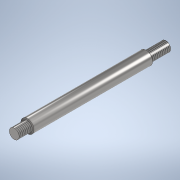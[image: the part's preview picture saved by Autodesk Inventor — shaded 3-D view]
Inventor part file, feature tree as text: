
AUTODESK INVENTOR PART (.ipt)
format: ipt  version: 2020 (Build 240168000, 168)  size: 111,104 bytes
history: native  units: mm
features: extrude x3, sketch x3, thread x1
ambient origin geometry x8: Origin, YZ Plane, XZ Plane, XY Plane, X Axis, Y Axis, Z Axis, Center Point
bodies: Solid1 (feature_tree)
feature tree (7):
  extrude  "Extrusion1"  Depth=6.0mm TaperAngle=0.0deg
  extrude  "Extrusion2"  Depth=36.0mm TaperAngle=0.0deg
  extrude  "Extrusion3"  Depth=4.0mm TaperAngle=0.0deg
  thread  "Thread1"  [1 undecoded]
  sketch  "Sketch1"  dims[d0=3.0mm d1=6.0mm d2=0.0mm]
  sketch  "Sketch2"  dims[d3=4.0mm d4=36.0mm d5=0.0mm]
  sketch  "Sketch3"  dims[d6=3.0mm d7=4.0mm d8=0.0mm d9=46.0mm d10=0.0mm]
note: 1 required parameter value undecoded (feature->parameter linkage not recoverable at this tier; creation-order binding heuristic only, values carry confidence <= 0.55)
